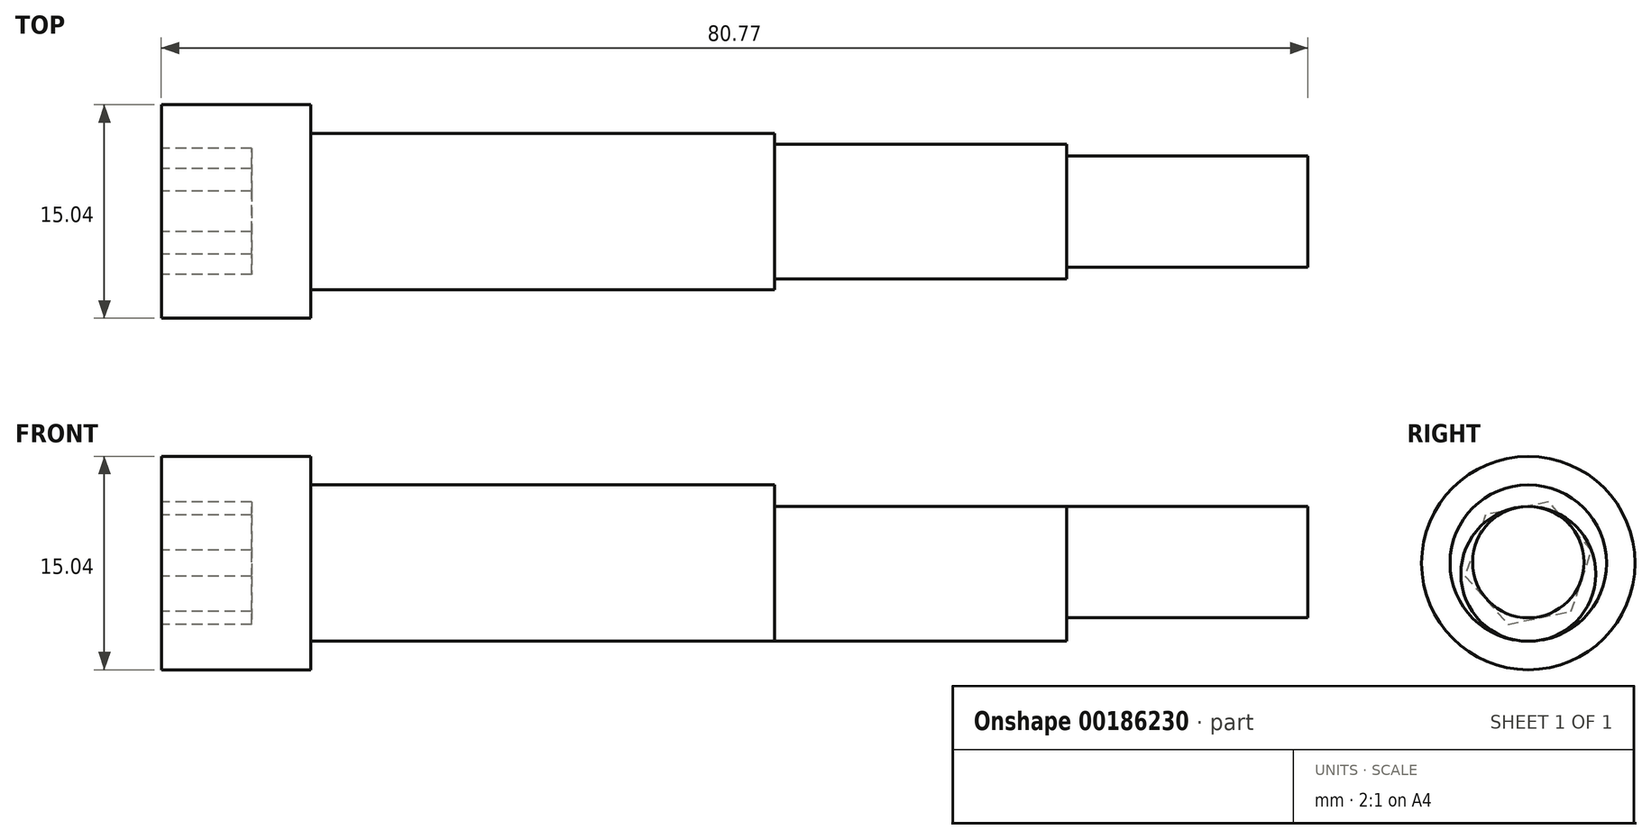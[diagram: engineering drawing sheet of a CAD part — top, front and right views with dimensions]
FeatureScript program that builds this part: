
annotation { "Feature Type Name" : "Feature", "Feature Type Description" : "" }
export const myFeature = defineFeature(function(context is Context, id is Id, definition is map)
    precondition{}
    {
        {
            var Q0;
            Q0=qCreatedBy(makeId("Front.planeOp"),FACE);
            var sketch = newSketch(context, id + "F0", { "sketchPlane" : qUnion([Q0])});
            skLineSegment(sketch, "E0", {"start": v(14.97, 25.2) * mm, "end": v(14.97, 10.16) * mm});
            skLineSegment(sketch, "E1", {"start": v(14.97, 25.2) * mm, "end": v(25.49, 25.2) * mm});
            skLineSegment(sketch, "E2", {"start": v(25.49, 25.2) * mm, "end": v(25.49, 23.2) * mm});
            skLineSegment(sketch, "E3", {"start": v(25.49, 23.2) * mm, "end": v(58.15, 23.2) * mm});
            skLineSegment(sketch, "E4", {"start": v(58.15, 23.2) * mm, "end": v(58.15, 21.67) * mm});
            skLineSegment(sketch, "E5", {"start": v(95.74, 21.67) * mm, "end": v(95.74, 13.82) * mm});
            skLineSegment(sketch, "E6", {"start": v(95.74, 13.82) * mm, "end": v(78.73, 13.82) * mm});
            skLineSegment(sketch, "E7", {"start": v(78.73, 13.82) * mm, "end": v(78.73, 12.17) * mm});
            skLineSegment(sketch, "E8", {"start": v(78.73, 12.17) * mm, "end": v(25.49, 12.17) * mm});
            skLineSegment(sketch, "E9", {"start": v(25.49, 12.17) * mm, "end": v(25.49, 10.16) * mm});
            skLineSegment(sketch, "E10", {"start": v(25.49, 10.16) * mm, "end": v(14.97, 10.16) * mm});
            skLineSegment(sketch, "E11", {"start": v(25.49, 23.2) * mm, "end": v(25.49, 12.17) * mm});
            skLineSegment(sketch, "E12", {"start": v(58.15, 21.67) * mm, "end": v(58.15, 12.17) * mm});
            skLineSegment(sketch, "E13", {"start": v(78.73, 13.82) * mm, "end": v(78.73, 21.67) * mm});
            skLineSegment(sketch, "E14", {"start": v(58.15, 21.67) * mm, "end": v(78.73, 21.67) * mm});
            skLineSegment(sketch, "E15", {"start": v(78.73, 21.67) * mm, "end": v(95.74, 21.67) * mm});
            skLineSegment(sketch, "E16", {"start": v(14.97, 17.68) * mm, "end": v(25.49, 17.68) * mm});
            skLineSegment(sketch, "E17", {"start": v(25.49, 17.68) * mm, "end": v(58.15, 17.68) * mm});
            skLineSegment(sketch, "E18", {"start": v(58.15, 17.68) * mm, "end": v(58.15, 16.92) * mm});
            skLineSegment(sketch, "E19", {"start": v(58.15, 16.92) * mm, "end": v(78.73, 16.92) * mm});
            skLineSegment(sketch, "E20", {"start": v(78.73, 16.92) * mm, "end": v(78.73, 17.75) * mm});
            skLineSegment(sketch, "E21", {"start": v(78.73, 17.75) * mm, "end": v(95.74, 17.75) * mm});
            skSolve(sketch);
        }
        {
            var Q0;
            {var subQ3=sQuery(id+"F0.wireOp",EDGE,"E1");Q0=makeQuery(id+"F0.imprint","IMPRINT",FACE,{"disambiguationData":[TD([[makeQuery(id+"F0.imprint","IMPRINT",EDGE,{"derivedFrom":subQ3}),-1.0]])]});}
            var Q1;
            Q1=sQuery(id+"F0.wireOp",EDGE,"E16");
            revolve(context, id + "F1", {"entities" : qUnion([Q0]), "axis" : qUnion([Q1]), "revolveType" : RevolveType.FULL});
        }
        {
            var Q0;
            {var subQ4=sQuery(id+"F0.wireOp",EDGE,"E3");Q0=makeQuery(id+"F0.imprint","IMPRINT",FACE,{"disambiguationData":[TD([[makeQuery(id+"F0.imprint","IMPRINT",EDGE,{"derivedFrom":subQ4}),-1.0]])]});}
            var Q1;
            Q1=sQuery(id+"F0.wireOp",EDGE,"E17");
            revolve(context, id + "F2", {"operationType" : NewBodyOperationType.ADD, "entities" : qUnion([Q0]), "axis" : qUnion([Q1]), "revolveType" : RevolveType.FULL});
        }
        {
            var Q0;
            {var subQ1=sQuery(id+"F0.wireOp",EDGE,"E14");Q0=makeQuery(id+"F0.imprint","IMPRINT",FACE,{"disambiguationData":[TD([[makeQuery(id+"F0.imprint","IMPRINT",EDGE,{"derivedFrom":subQ1}),-1.0]])]});}
            var Q1;
            Q1=sQuery(id+"F0.wireOp",EDGE,"E19");
            revolve(context, id + "F3", {"operationType" : NewBodyOperationType.ADD, "entities" : qUnion([Q0]), "axis" : qUnion([Q1]), "revolveType" : RevolveType.FULL});
        }
        {
            var Q0;
            {var subQ0=sQuery(id+"F0.wireOp",EDGE,"E15");Q0=makeQuery(id+"F0.imprint","IMPRINT",FACE,{"disambiguationData":[TD([[makeQuery(id+"F0.imprint","IMPRINT",EDGE,{"derivedFrom":subQ0}),-1.0]])]});}
            var Q1;
            Q1=sQuery(id+"F0.wireOp",EDGE,"E21");
            revolve(context, id + "F4", {"operationType" : NewBodyOperationType.ADD, "entities" : qUnion([Q0]), "axis" : qUnion([Q1]), "revolveType" : RevolveType.FULL});
        }
        {
            var Q0;
            Q0=makeQuery(id+"F1.opRevolve","SWEPT_FACE",FACE,{"disambiguationData":[OSD([sQuery(id+"F0.wireOp",EDGE,"E0")])]});
            var sketch = newSketch(context, id + "F5", { "sketchPlane" : qUnion([Q0])});
            skCircle(sketch, "E22.cCircle", {"center": v(0, 17.68) * mm, "radius": 4.55 * mm, "construction": true});
            skLineSegment(sketch, "E22.0", {"start": v(4.45, 16.77) * mm, "end": v(1.44, 13.37) * mm});
            skLineSegment(sketch, "E22.1", {"start": v(1.44, 13.37) * mm, "end": v(-3.02, 14.28) * mm});
            skLineSegment(sketch, "E22.2", {"start": v(-3.02, 14.28) * mm, "end": v(-4.45, 18.6) * mm});
            skLineSegment(sketch, "E22.3", {"start": v(-4.45, 18.6) * mm, "end": v(-1.44, 22) * mm});
            skLineSegment(sketch, "E22.4", {"start": v(-1.44, 22) * mm, "end": v(3.02, 21.08) * mm});
            skLineSegment(sketch, "E22.5", {"start": v(3.02, 21.08) * mm, "end": v(4.45, 16.77) * mm});
            skSolve(sketch);
        }
        {
            var Q0;
            Q0=makeQuery(id+"F5.imprint","IMPRINT",FACE,{"disambiguationData":[TD([[makeQuery(id+"F5.imprint","IMPRINT",EDGE,{"derivedFrom":sQuery(id+"F5.wireOp",EDGE,"E22.0")}),-1.0]])]});
            extrude(context, id + "F6", {"entities" : qUnion([Q0]), "operationType" : NewBodyOperationType.REMOVE, "oppositeDirection" : true, "depth" : 6.35 * mm});
        }
    });
